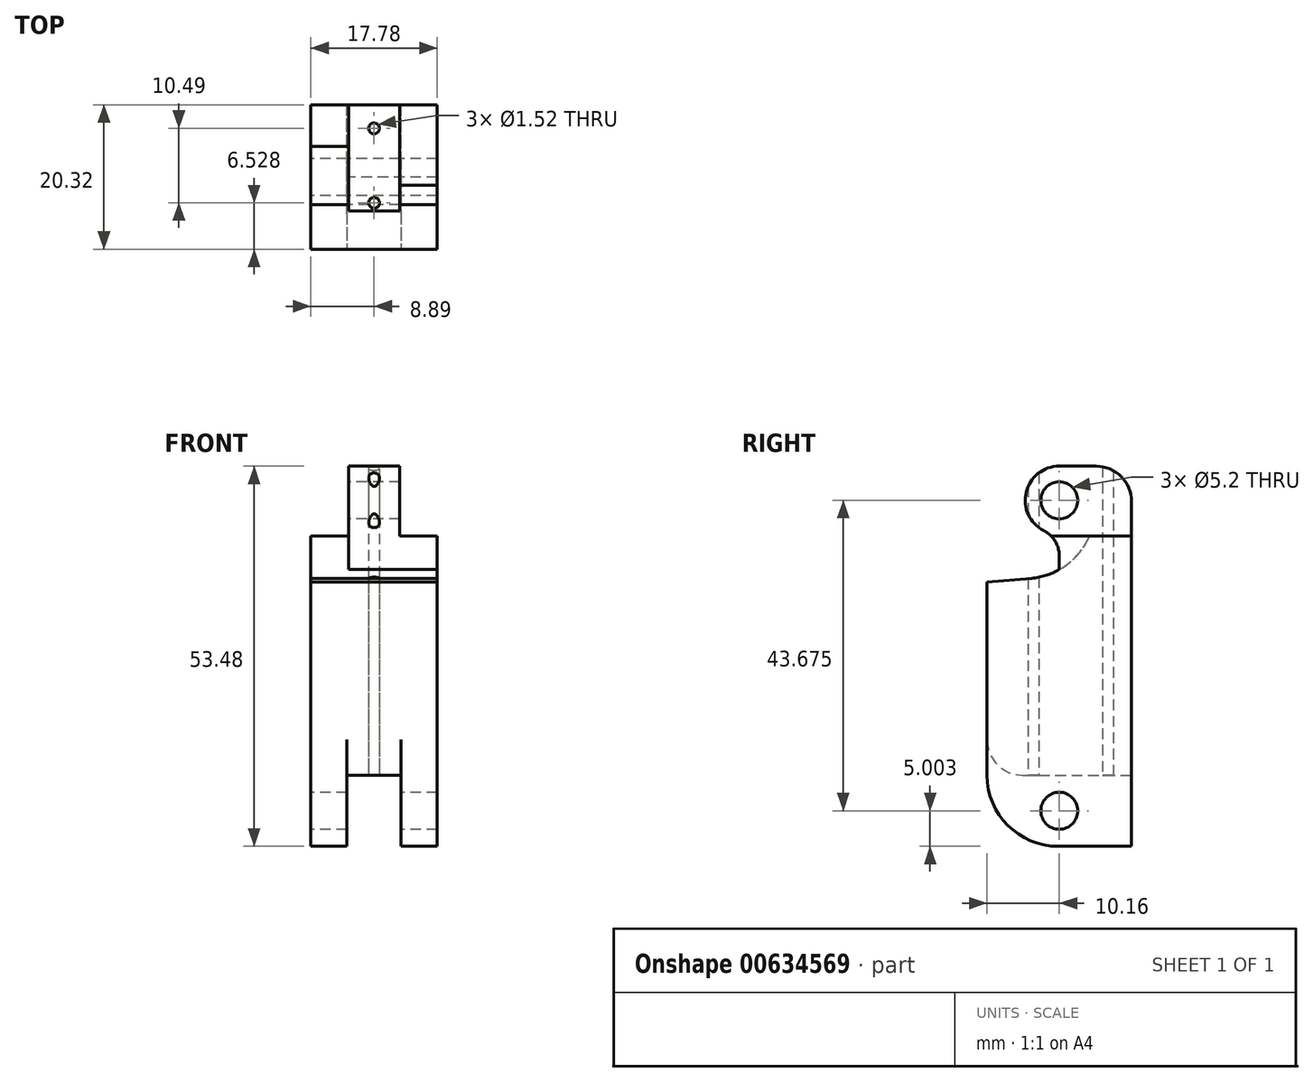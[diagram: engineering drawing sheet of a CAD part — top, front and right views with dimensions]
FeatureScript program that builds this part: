
annotation { "Feature Type Name" : "Feature", "Feature Type Description" : "" }
export const myFeature = defineFeature(function(context is Context, id is Id, definition is map)
    precondition{}
    {
        {
            var Q0;
            Q0=qCreatedBy(makeId("Front.planeOp"),FACE);
            var sketch = newSketch(context, id + "F0", { "sketchPlane" : qUnion([Q0])});
            skLineSegment(sketch, "E0.bottom", {"start": v(8.9, 21.84) * mm, "end": v(3.61, 21.84) * mm});
            skLineSegment(sketch, "E0.top", {"start": v(8.9, -21.84) * mm, "end": v(3.81, -21.84) * mm});
            skLineSegment(sketch, "E0.left", {"start": v(8.89, 21.84) * mm, "end": v(8.89, -21.84) * mm});
            skLineSegment(sketch, "E0.right", {"start": v(-8.9, 21.84) * mm, "end": v(-8.9, -21.84) * mm});
            skPoint(sketch, "E0.middle", {"position": v(0, 0) * mm});
            skLineSegment(sketch, "E1.left", {"start": v(3.81, -21.84) * mm, "end": v(3.81, -11.84) * mm});
            skLineSegment(sketch, "E1.right", {"start": v(-3.81, -21.84) * mm, "end": v(-3.81, -11.84) * mm});
            skLineSegment(sketch, "E2", {"start": v(0, -11.84) * mm, "end": v(3.81, -11.84) * mm});
            skLineSegment(sketch, "E3", {"start": v(0, -11.84) * mm, "end": v(-3.81, -11.84) * mm});
            skLineSegment(sketch, "E4.trimOffspring", {"start": v(-3.81, -21.84) * mm, "end": v(-8.9, -21.84) * mm});
            skLineSegment(sketch, "E5.bottom", {"start": v(3.6, 31.64) * mm, "end": v(-3.61, 31.64) * mm});
            skLineSegment(sketch, "E5.left", {"start": v(3.6, 31.64) * mm, "end": v(3.6, 21.84) * mm});
            skLineSegment(sketch, "E5.right", {"start": v(-3.61, 31.64) * mm, "end": v(-3.61, 21.84) * mm});
            skPoint(sketch, "E5.middle", {"position": v(0, 21.84) * mm});
            skLineSegment(sketch, "E6.trimOffspring", {"start": v(-3.61, 21.84) * mm, "end": v(-8.9, 21.84) * mm});
            skPoint(sketch, "E7.orphan", {"position": v(-3.6, 12.04) * mm});
            skPoint(sketch, "E8.orphan", {"position": v(3.6, 12.04) * mm});
            skSolve(sketch);
        }
        {
            var Q0;
            Q0=makeQuery(id+"F0.imprint","IMPRINT",FACE,{"disambiguationData":[TD([[makeQuery(id+"F0.imprint","IMPRINT",EDGE,{"derivedFrom":sQuery(id+"F0.wireOp",EDGE,"E0.bottom")}),1.0]])]});
            extrude(context, id + "F1", {"entities" : qUnion([Q0]), "endBound" : BoundingType.SYMMETRIC, "depth" : 20.32 * mm, "offsetDistance" : 25.4 * mm});
        }
        {
            var Q0;
            Q0=makeQuery(id+"F1.opExtrude","SWEPT_FACE",FACE,{"disambiguationData":[OSD([sQuery(id+"F0.wireOp",EDGE,"E0.right")])]});
            var sketch = newSketch(context, id + "F2", { "sketchPlane" : qUnion([Q0])});
            skPoint(sketch, "E9.endSnap0", {"position": v(0, -21.84) * mm});
            skCircle(sketch, "E10", {"center": v(0, -16.84) * mm, "radius": 2.6 * mm});
            skSolve(sketch);
        }
        {
            var Q0;
            Q0=makeQuery(id+"F2.imprint","IMPRINT",FACE,{"disambiguationData":[TD([[makeQuery(id+"F2.imprint","IMPRINT",EDGE,{"derivedFrom":sQuery(id+"F2.wireOp",EDGE,"E10")}),1.0]])]});
            extrude(context, id + "F3", {"entities" : qUnion([Q0]), "operationType" : NewBodyOperationType.REMOVE, "endBound" : BoundingType.THROUGH_ALL, "oppositeDirection" : true, "depth" : 25.4 * mm, "offsetDistance" : 25.4 * mm});
        }
        {
            var Q0;
            Q0=makeQuery(id+"F1.opExtrude","SWEPT_FACE",FACE,{"disambiguationData":[OSD([sQuery(id+"F0.wireOp",EDGE,"E0.right")])]});
            var sketch = newSketch(context, id + "F4", { "sketchPlane" : qUnion([Q0])});
            skLineSegment(sketch, "E11", {"start": v(10.16, 21.84) * mm, "end": v(-4.3, 21.84) * mm});
            skLineSegment(sketch, "E12", {"start": v(10.16, 21.84) * mm, "end": v(10.16, 15.3) * mm});
            skLineSegment(sketch, "E13", {"start": v(10.16, 15.3) * mm, "end": v(3.89, 15.86) * mm});
            skPoint(sketch, "E14.visualSharp", {"position": v(-2.14, 14.35) * mm});
            skArc(sketch, "E14.filletArc", {"start": v(-4.3, 21.84) * mm, "mid": v(-1.02, 17.74) * mm, "end": v(3.89, 15.86) * mm});
            skSolve(sketch);
        }
        {
            var Q0;
            Q0=makeQuery(id+"F4.imprint","IMPRINT",FACE,{"disambiguationData":[TD([[makeQuery(id+"F4.imprint","IMPRINT",EDGE,{"derivedFrom":sQuery(id+"F4.wireOp",EDGE,"E11")}),1.0]])]});
            extrude(context, id + "F5", {"entities" : qUnion([Q0]), "operationType" : NewBodyOperationType.REMOVE, "oppositeDirection" : true, "depth" : 5.08 * mm + .2 * mm, "offsetDistance" : 25.4 * mm});
        }
        {
            var Q0;
            Q0=makeQuery(id+"F1.opExtrude","CAP_EDGE",EDGE,{"disambiguationData":[OSD([sQuery(id+"F0.wireOp",EDGE,"E0.top")])],"isStart":false});
            var Q1;
            Q1=makeQuery(id+"F1.opExtrude","CAP_EDGE",EDGE,{"disambiguationData":[OSD([sQuery(id+"F0.wireOp",EDGE,"E4.trimOffspring")])],"isStart":false});
            fillet(context, id + "F6", {"entities" : qUnion([Q0, Q1]), "radius" : 10 * mm, "tangentPropagation" : true, "allowEdgeOverflow" : false});
        }
        {
            var Q0;
            Q0=makeQuery(id+"F5.boolean.opBoolean","MERGE",FACE,{"derivedFrom":[makeQuery(id+"F1.opExtrude","SWEPT_FACE",FACE,{"disambiguationData":[OSD([sQuery(id+"F0.wireOp",EDGE,"E5.right")])]}),makeQuery(id+"F5.opExtrude","CAP_FACE",FACE,{"disambiguationData":[OSD([sQuery(id+"F4.wireOp",EDGE,"E11"),sQuery(id+"F4.wireOp",EDGE,"E12"),sQuery(id+"F4.wireOp",EDGE,"E13"),sQuery(id+"F4.wireOp",EDGE,"E14.filletArc")])],"isStart":false})]});
            var sketch = newSketch(context, id + "F7", { "sketchPlane" : qUnion([Q0])});
            skLineSegment(sketch, "E15", {"start": v(0, 21.84) * mm, "end": v(0, 22.04) * mm});
            skCircle(sketch, "E16", {"center": v(0, 26.84) * mm, "radius": 2.6 * mm});
            skArc(sketch, "E17", {"start": v(0, 22.04) * mm, "mid": v(4.8, 26.84) * mm, "end": v(0, 31.64) * mm});
            skLineSegment(sketch, "E18", {"start": v(0, 31.64) * mm, "end": v(10.16, 31.64) * mm});
            skLineSegment(sketch, "E19", {"start": v(10.16, 31.64) * mm, "end": v(10.16, 15.3) * mm});
            skLineSegment(sketch, "E20", {"start": v(0, 21.84) * mm, "end": v(0, 17.08) * mm});
            skArc(sketch, "E21", {"start": v(0, 17.08) * mm, "mid": v(2, 16.23) * mm, "end": v(4.14, 15.84) * mm});
            skPoint(sketch, "E21.first.point", {"position": v(-4.3, 21.84) * mm});
            skPoint(sketch, "E21.third.point", {"position": v(13.07, 31.55) * mm});
            skLineSegment(sketch, "E22", {"start": v(10.16, 15.3) * mm, "end": v(3.89, 15.86) * mm});
            skArc(sketch, "E23.trimOffspring", {"start": v(-4.3, 21.84) * mm, "mid": v(-1.02, 17.74) * mm, "end": v(3.89, 15.86) * mm});
            skSolve(sketch);
        }
        {
            var Q0;
            Q0=makeQuery(id+"F7.imprint","IMPRINT",FACE,{"disambiguationData":[TD([[makeQuery(id+"F7.imprint","IMPRINT",EDGE,{"derivedFrom":sQuery(id+"F7.wireOp",EDGE,"E16")}),1.0]])]});
            var Q1;
            Q1=makeQuery(id+"F7.imprint","IMPRINT",FACE,{"disambiguationData":[TD([[makeQuery(id+"F7.imprint","IMPRINT",EDGE,{"derivedFrom":sQuery(id+"F7.wireOp",EDGE,"E15")}),-1.0]])]});
            extrude(context, id + "F8", {"entities" : qUnion([Q0, Q1]), "operationType" : NewBodyOperationType.REMOVE, "endBound" : BoundingType.THROUGH_ALL, "oppositeDirection" : true, "depth" : 25.4 * mm, "offsetDistance" : 25.4 * mm});
        }
        {
            var Q0;
            Q0=makeQuery(id+"F8.boolean.opBoolean","COPY",EDGE,{"derivedFrom":makeQuery(id+"F8.opExtrude","SWEPT_EDGE",EDGE,{"disambiguationData":[OSD([sQuery(id+"F7.wireOp",EDGE,"E15"),sQuery(id+"F7.wireOp",EDGE,"E17")])]})});
            var Q1;
            Q1=makeQuery(id+"F8.boolean.opBoolean","COPY",EDGE,{"derivedFrom":makeQuery(id+"F8.opExtrude","SWEPT_EDGE",EDGE,{"disambiguationData":[OSD([sQuery(id+"F7.wireOp",EDGE,"E20"),sQuery(id+"F7.wireOp",EDGE,"E22")])]})});
            fillet(context, id + "F9", {"entities" : qUnion([Q0, Q1]), "radius" : 4 * mm, "tangentPropagation" : true, "allowEdgeOverflow" : false});
        }
        {
            var Q0;
            Q0=makeQuery(id+"F1.opExtrude","CAP_EDGE",EDGE,{"disambiguationData":[OSD([sQuery(id+"F0.wireOp",EDGE,"E5.bottom")])],"isStart":true});
            fillet(context, id + "F10", {"entities" : qUnion([Q0]), "radius" : 5 * mm, "tangentPropagation" : true, "allowEdgeOverflow" : false});
        }
        {
            var Q0;
            Q0=makeQuery(id+"F1.opExtrude","CAP_EDGE",EDGE,{"disambiguationData":[OSD([sQuery(id+"F0.wireOp",EDGE,"E2"),sQuery(id+"F0.wireOp",EDGE,"E3")])],"isStart":false});
            fillet(context, id + "F11", {"entities" : qUnion([Q0]), "radius" : 5 * mm, "tangentPropagation" : true, "allowEdgeOverflow" : false});
        }
        {
            var Q0;
            Q0=makeQuery(id+"F1.opExtrude","SWEPT_FACE",FACE,{"disambiguationData":[OSD([sQuery(id+"F0.wireOp",EDGE,"E2"),sQuery(id+"F0.wireOp",EDGE,"E3")])]});
            var sketch = newSketch(context, id + "F12", { "sketchPlane" : qUnion([Q0])});
            skLineSegment(sketch, "E24", {"start": v(0, -10.16) * mm, "end": v(0, -7.62) * mm});
            skPoint(sketch, "E24.endSnap0", {"position": v(0, -10.16) * mm});
            skCircle(sketch, "E25", {"center": v(0, -6.86) * mm, "radius": 0.76 * mm});
            skLineSegment(sketch, "E26", {"start": v(0, 10.16) * mm, "end": v(0, 4.4) * mm});
            skCircle(sketch, "E27", {"center": v(0, 3.63) * mm, "radius": 0.76 * mm});
            skLineSegment(sketch, "E28", {"start": v(-8.9, 10.16) * mm, "end": v(8.89, 10.16) * mm});
            skSolve(sketch);
        }
        {
            var Q0;
            Q0=makeQuery(id+"F12.imprint","IMPRINT",FACE,{"disambiguationData":[TD([[makeQuery(id+"F12.imprint","IMPRINT",EDGE,{"derivedFrom":sQuery(id+"F12.wireOp",EDGE,"E27")}),1.0]])]});
            var Q1;
            Q1=makeQuery(id+"F12.imprint","IMPRINT",FACE,{"disambiguationData":[TD([[makeQuery(id+"F12.imprint","IMPRINT",EDGE,{"derivedFrom":sQuery(id+"F12.wireOp",EDGE,"E25")}),1.0]])]});
            extrude(context, id + "F13", {"entities" : qUnion([Q0, Q1]), "operationType" : NewBodyOperationType.REMOVE, "endBound" : BoundingType.THROUGH_ALL, "oppositeDirection" : true, "depth" : 25.4 * mm, "offsetDistance" : 25.4 * mm});
        }
    });
